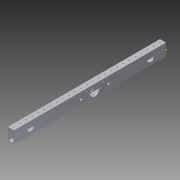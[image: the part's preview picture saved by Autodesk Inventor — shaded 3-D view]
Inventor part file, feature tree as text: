
AUTODESK INVENTOR PART (.ipt)
format: ipt  version: 2014 (Build 180170000, 170)  size: 486,400 bytes
history: native  units: in
note: dims shown in document units (in); Inventor stores cm internally (conversion verified against a paired STEP export)
features: extrude x10, sketch x9, reference x4, pattern_linear x1
ambient origin geometry x8: Origin, YZ Plane, XZ Plane, XY Plane, X Axis, Y Axis, Z Axis, Center Point
bodies: Solid1 (feature_tree)
feature tree (24):
  extrude  "Extrusion1"  Depth=2.0in
  extrude  "Extrusion2"  Depth=0.1in TaperAngle=0.0deg
  extrude  "Extrusion3"  Depth=1.0in
  extrude  "Extrusion4"  Depth=1.0in TaperAngle=0.0deg
  extrude  "Extrusion5"  Depth=1.125in
  extrude  "Extrusion6"  Depth=0.125in
  extrude  "Extrusion7"  Depth=27.0in TaperAngle=0.0deg
  extrude  "Extrusion8"  Depth=0.2in
  pattern_linear  "Rectangular Pattern1"  Spacing1=0.2in  [1 undecoded]
  extrude  "Extrusion9"  Depth=1.0in
  extrude  "Extrusion10"  Depth=1.0in
  sketch  "Sketch1"  dims[d0=1.0in d1=2.0in]
  sketch  "Sketch2"  dims[d2=0.1in d3=27.0in d4=0.0in]
  sketch  "Sketch3"  dims[d5=1.0in d6=1.0in]
  sketch  "Sketch5"  dims[d7=1.0in d8=27.0in d9=0.0in]
  reference  "Reference1"
  reference  "Reference2"
  reference  "Reference3"
  reference  "Reference4"
  sketch  "Sketch6"  dims[d11=1.0625in d12=1.125in]
  sketch  "Sketch7"  dims[d14=1.125in d16=0.125in]
  sketch  "Sketch8"  dims[d18=1.5in d19=27.0in d20=0.0in]
  sketch  "Sketch9"  dims[d21=0.938in d22=0.2in]
  sketch  "Sketch10"  dims[d23=0.938in d24=0.2in d25=2.25in d26=2.25in d27=0.4in d28=1.0in d29=0.0in d30=1.0in d31=0.0in d32=0.5in d33=0.003in d34=135.0deg d35=135.0deg d36=0.003in d37=135.0deg d38=135.0deg d39=0.5in d40=0.003in d41=0.003in d42=0.003in d43=0.003in d44=27.0in d45=0.0in d46=135.0deg d47=135.0deg d48=0.5in d50=0.003in d51=0.003in d52=27.0in d53=0.0in d54=0.003in d55=0.5in d56=0.164in d57=27.0in d58=0.0in d59=10.6299in d61=1.0in d62=1.0in d63=1.0in d64=1.0in d65=1.0in d66=1.0in d67=0.0in d68=9.2in d70=10.55in d71=2.5in d72=2.75in d73=0.0625in d74=0.0625in d81=1.0in d82=0.0in d83=1.0625in d84=1.0625in d85=1.3262in d86=1.3262in d87=0.1339in d88=0.1339in]
note: 1 required parameter value undecoded (feature->parameter linkage not recoverable at this tier; creation-order binding heuristic only, values carry confidence <= 0.55)
